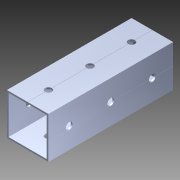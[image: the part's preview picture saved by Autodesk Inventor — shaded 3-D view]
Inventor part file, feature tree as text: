
AUTODESK INVENTOR PART (.ipt)
format: ipt  version: 2014 SP1 (Build 180222100, 222)  size: 1,242,112 bytes
history: native  units: in
note: dims shown in document units (in); Inventor stores cm internally (conversion verified against a paired STEP export)
features: extrude x4, sketch x4, pattern_circular x1, other x1, imported_body x1
ambient origin geometry x8: Origin, YZ Plane, XZ Plane, XY Plane, X Axis, Y Axis, Z Axis, Center Point
bodies: Body1 (feature_tree)
feature tree (11):
  pattern_circular  "CirPattern2"
  other  "1x1 tube1"
  extrude  "Extrusion1"  Depth=4.0in TaperAngle=0.0deg
  extrude  "Extrusion2"  Depth=1.0in TaperAngle=0.0deg
  extrude  "Extrusion3"  [1 undecoded]
  extrude  "Extrusion4"  [1 undecoded]
  imported_body  "Base1"
  sketch  "Sketch1"  dims[d0=50.0in d1=0.0in d2=4.0in d3=0.0in]
  sketch  "Sketch3"  dims[d4=1.0in d5=0.0in d6=1.0in d7=0.0in]
  sketch  "Sketch4"
  sketch  "Sketch5"
note: 2 required parameter values undecoded (feature->parameter linkage not recoverable at this tier; creation-order binding heuristic only, values carry confidence <= 0.55)
